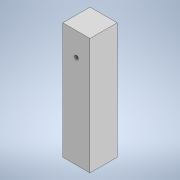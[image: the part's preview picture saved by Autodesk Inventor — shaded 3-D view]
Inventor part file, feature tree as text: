
AUTODESK INVENTOR PART (.ipt)
format: ipt  version: 2021 (Build 250183000, 183)  size: 99,840 bytes
history: native  units: in
note: dims shown in document units (in); Inventor stores cm internally (conversion verified against a paired STEP export)
features: extrude x2, sketch x2
ambient origin geometry x8: Origin, YZ Plane, XZ Plane, XY Plane, X Axis, Y Axis, Z Axis, Center Point
bodies: Solid1 (feature_tree)
feature tree (4):
  extrude  "Extrusion1"  Depth=3.5in
  extrude  "Extrusion2"  Depth=3.5in TaperAngle=0.0deg
  sketch  "Sketch1"  dims[d0=15.0in d1=3.5in]
  sketch  "Sketch2"  dims[d2=3.5in d3=3.5in d4=0.0in d5=0.5in d6=1.75in d7=3.0in d8=3.5in d9=0.0in]
